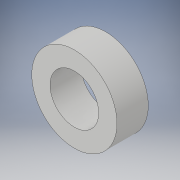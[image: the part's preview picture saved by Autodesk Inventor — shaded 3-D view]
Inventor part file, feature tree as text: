
AUTODESK INVENTOR PART (.ipt)
format: ipt  version: 2019 (Build 230136000, 136)  size: 101,376 bytes
history: native  units: mm
features: extrude x2, sketch x2
ambient origin geometry x8: Origin, YZ Plane, XZ Plane, XY Plane, X Axis, Y Axis, Z Axis, Center Point
bodies: Solid1 (feature_tree)
feature tree (4):
  extrude  "Extrusion1"  Depth=14.4mm TaperAngle=0.0deg
  extrude  "Extrusion2"  Depth=14.4mm TaperAngle=0.0deg
  sketch  "Sketch1"  dims[d0=39.2mm d1=14.4mm d2=0.0mm]
  sketch  "Sketch2"  dims[d3=22.4mm d4=14.4mm d5=0.0mm]
